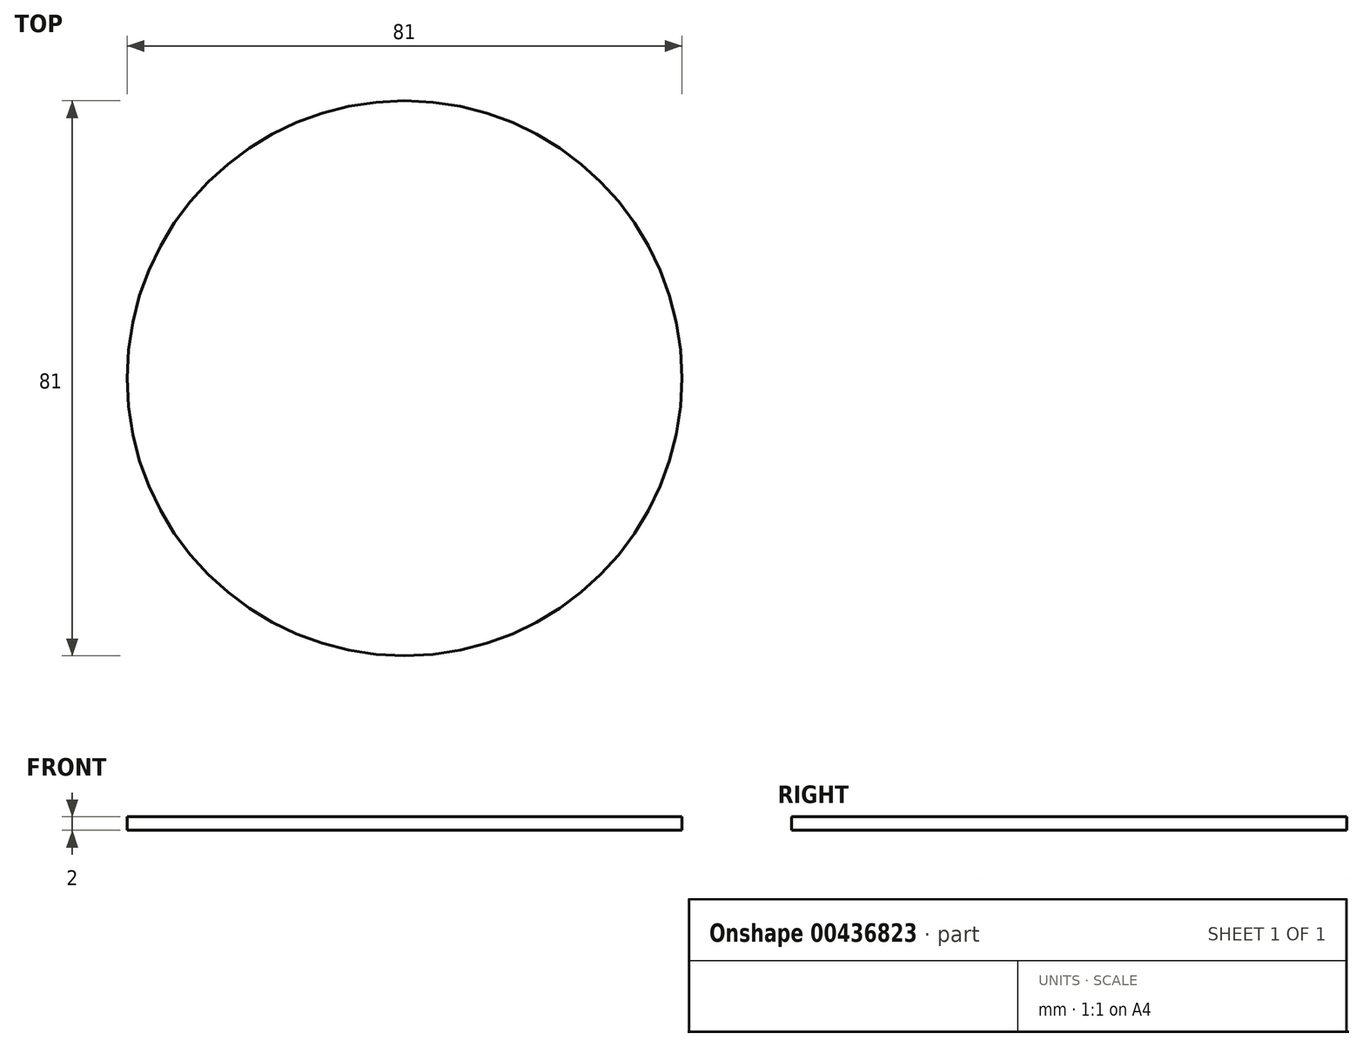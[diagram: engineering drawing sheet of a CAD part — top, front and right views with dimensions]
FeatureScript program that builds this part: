
annotation { "Feature Type Name" : "Feature", "Feature Type Description" : "" }
export const myFeature = defineFeature(function(context is Context, id is Id, definition is map)
    precondition{}
    {
        {
            var Q0;
            Q0=qCreatedBy(makeId("Top.planeOp"),FACE);
            var sketch = newSketch(context, id + "F0", { "sketchPlane" : qUnion([Q0])});
            skCircle(sketch, "E0", {"center": v(0, 0) * mm, "radius": 40.5 * mm});
            skSolve(sketch);
        }
        {
            var Q0;
            Q0=makeQuery(id+"F0.imprint","IMPRINT",FACE,{"disambiguationData":[TD([[makeQuery(id+"F0.imprint","IMPRINT",EDGE,{"derivedFrom":sQuery(id+"F0.wireOp",EDGE,"E0")}),1.0]])]});
            extrude(context, id + "F1", {"entities" : qUnion([Q0]), "depth" : 2 * mm});
        }
    });
